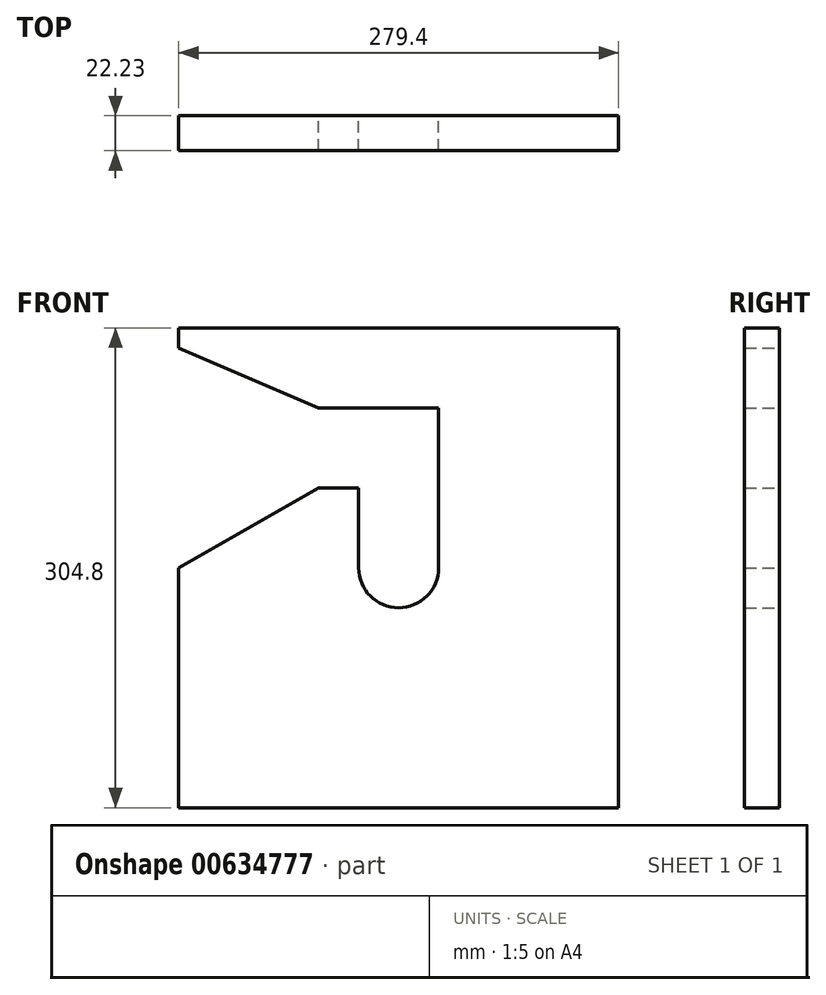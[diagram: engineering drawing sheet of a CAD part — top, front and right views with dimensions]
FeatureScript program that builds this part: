
annotation { "Feature Type Name" : "Feature", "Feature Type Description" : "" }
export const myFeature = defineFeature(function(context is Context, id is Id, definition is map)
    precondition{}
    {
        {
            var Q0;
            Q0=qCreatedBy(makeId("Front.planeOp"),FACE);
            var sketch = newSketch(context, id + "F0", { "sketchPlane" : qUnion([Q0])});
            skLineSegment(sketch, "E0.bottom", {"start": v(139.7, 152.4) * mm, "end": v(-139.7, 152.4) * mm});
            skLineSegment(sketch, "E0.top", {"start": v(139.7, -152.4) * mm, "end": v(-139.7, -152.4) * mm});
            skLineSegment(sketch, "E0.left", {"start": v(139.7, 152.4) * mm, "end": v(139.7, -152.4) * mm});
            skLineSegment(sketch, "E0.right", {"start": v(-139.7, 152.4) * mm, "end": v(-139.7, 139.7) * mm});
            skPoint(sketch, "E0.middle", {"position": v(0, 0) * mm});
            skArc(sketch, "E1", {"start": v(-25.4, 0) * mm, "mid": v(0, -25.4) * mm, "end": v(25.4, 0) * mm});
            skLineSegment(sketch, "E2.top", {"start": v(25.4, 101.6) * mm, "end": v(-25.4, 101.6) * mm});
            skLineSegment(sketch, "E2.left", {"start": v(25.4, 0) * mm, "end": v(25.4, 101.6) * mm});
            skLineSegment(sketch, "E2.right", {"start": v(-25.4, 0) * mm, "end": v(-25.4, 50.8) * mm});
            skLineSegment(sketch, "E3.bottom", {"start": v(25.4, 101.6) * mm, "end": v(-50.8, 101.6) * mm});
            skLineSegment(sketch, "E3.top", {"start": v(-25.4, 50.8) * mm, "end": v(-50.8, 50.8) * mm});
            skLineSegment(sketch, "E3.left", {"start": v(25.4, 101.6) * mm, "end": v(25.4, 50.8) * mm});
            skLineSegment(sketch, "E4", {"start": v(-50.8, 101.6) * mm, "end": v(-139.7, 139.7) * mm});
            skLineSegment(sketch, "E5", {"start": v(-50.8, 50.8) * mm, "end": v(-139.7, 0) * mm});
            skLineSegment(sketch, "E6.trimOffspring", {"start": v(-139.7, 0) * mm, "end": v(-139.7, -152.4) * mm});
            skSolve(sketch);
        }
        {
            var Q0;
            Q0 = qSketchRegion(id + "F0", true);
            extrude(context, id + "F1", {"entities" : qUnion([Q0]), "depth" : 22.22 * mm, "offsetDistance" : 25.4 * mm});
        }
    });
